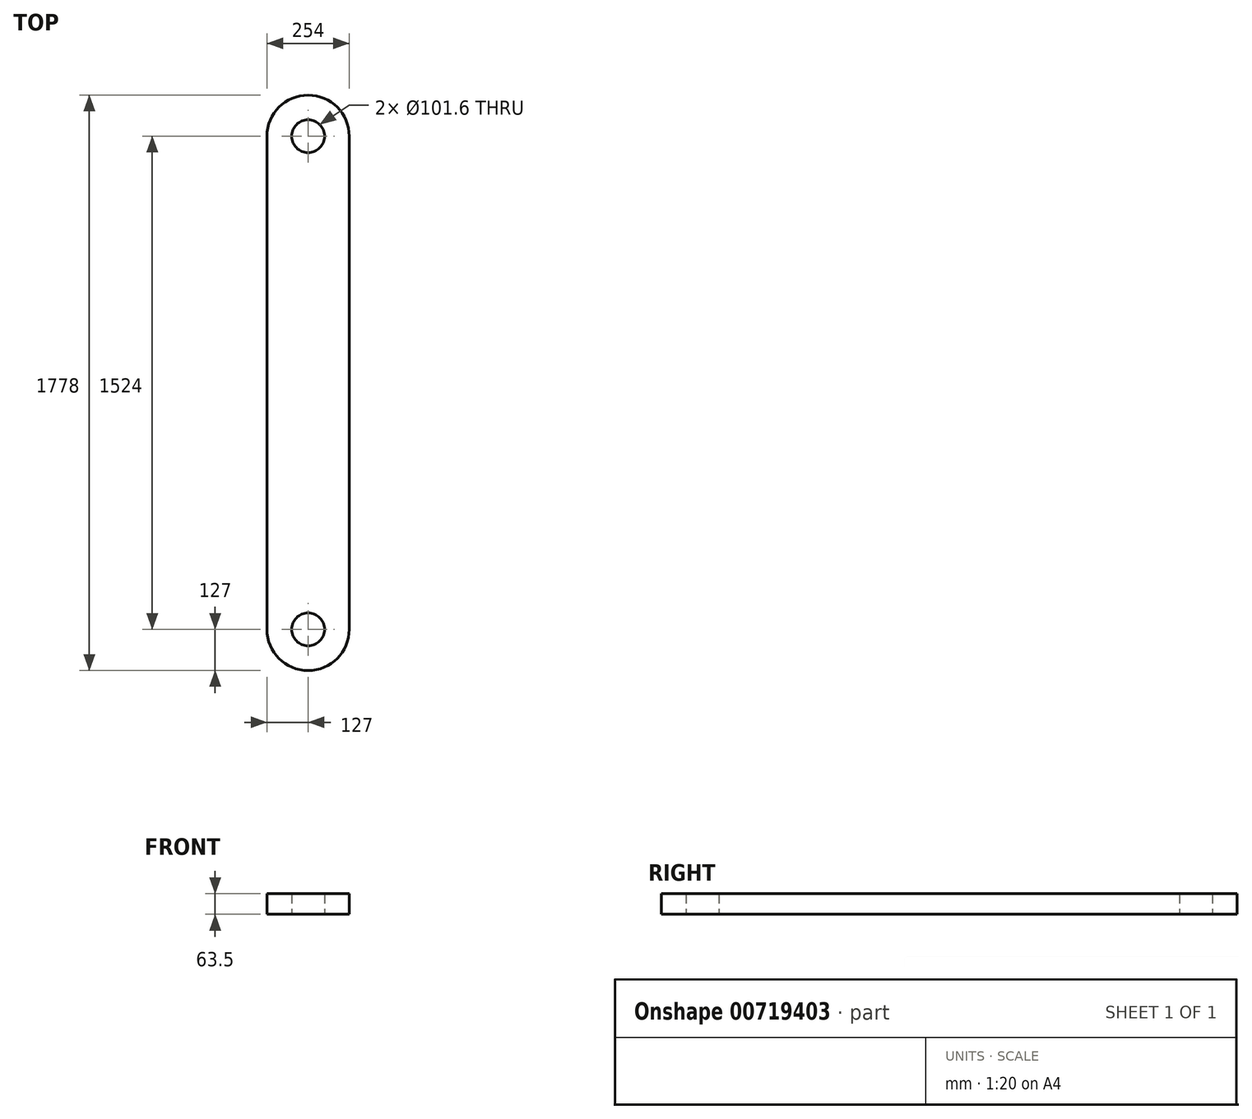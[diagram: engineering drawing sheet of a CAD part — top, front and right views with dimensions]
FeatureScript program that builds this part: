
annotation { "Feature Type Name" : "Feature", "Feature Type Description" : "" }
export const myFeature = defineFeature(function(context is Context, id is Id, definition is map)
    precondition{}
    {
        {
            var Q0;
            Q0=qCreatedBy(makeId("Top.planeOp"),FACE);
            var sketch = newSketch(context, id + "F0", { "sketchPlane" : qUnion([Q0])});
            skArc(sketch, "E0", {"start": v(127, 762) * mm, "mid": v(0, 889) * mm, "end": v(-127, 762) * mm});
            skArc(sketch, "E1", {"start": v(-127, -762) * mm, "mid": v(0, -889) * mm, "end": v(127, -762) * mm});
            skLineSegment(sketch, "E2", {"start": v(127, 762) * mm, "end": v(127, -762) * mm});
            skLineSegment(sketch, "E3", {"start": v(-127, 762) * mm, "end": v(-127, -762) * mm});
            skCircle(sketch, "E4", {"center": v(0, 762) * mm, "radius": 50.8 * mm});
            skCircle(sketch, "E5", {"center": v(0, -762) * mm, "radius": 50.8 * mm});
            skSolve(sketch);
        }
        {
            var Q0;
            Q0 = qSketchRegion(id + "F0", true);
            extrude(context, id + "F1", {"entities" : qUnion([Q0]), "depth" : 63.5 * mm, "offsetDistance" : 25.4 * mm});
        }
    });
